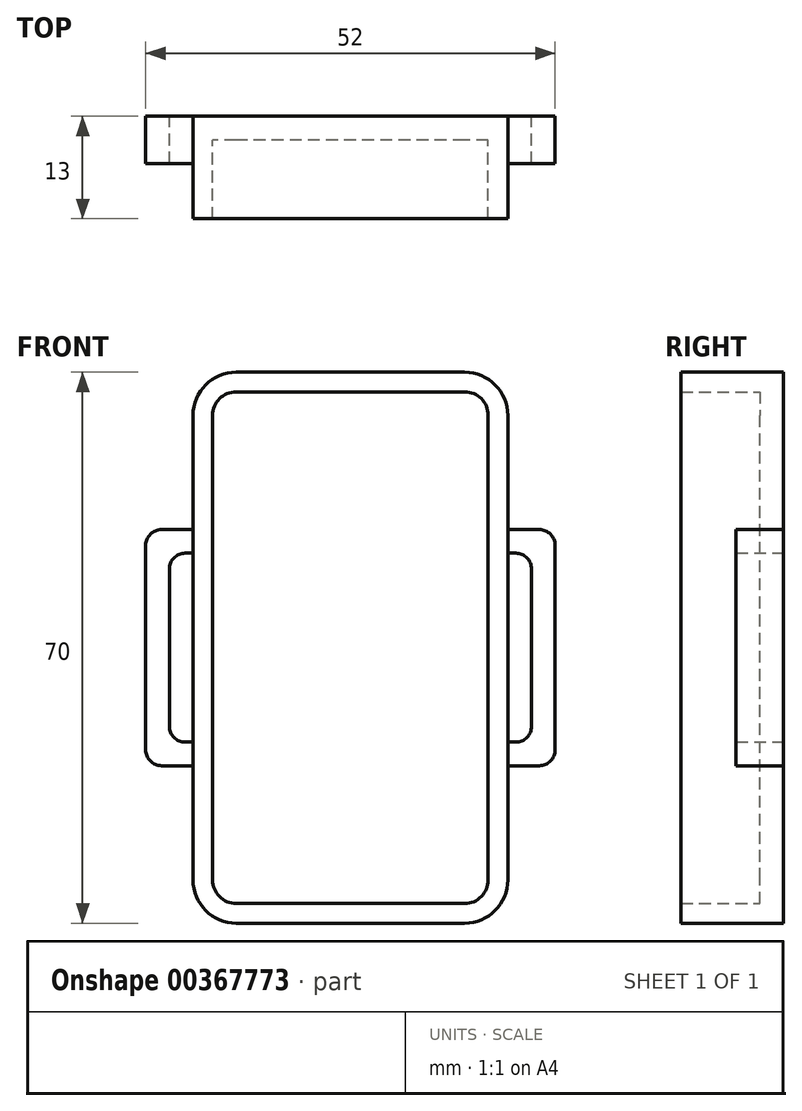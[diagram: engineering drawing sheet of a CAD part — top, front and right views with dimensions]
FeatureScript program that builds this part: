
annotation { "Feature Type Name" : "Feature", "Feature Type Description" : "" }
export const myFeature = defineFeature(function(context is Context, id is Id, definition is map)
    precondition{}
    {
        {
            var Q0;
            Q0=qCreatedBy(makeId("Front.planeOp"),FACE);
            var sketch = newSketch(context, id + "F0", { "sketchPlane" : qUnion([Q0])});
            skLineSegment(sketch, "E0.bottom", {"start": v(14.5, -32.5) * mm, "end": v(-14.5, -32.5) * mm});
            skLineSegment(sketch, "E0.top", {"start": v(14.5, 32.5) * mm, "end": v(-14.5, 32.5) * mm});
            skLineSegment(sketch, "E0.left", {"start": v(17.5, -29.5) * mm, "end": v(17.5, 29.5) * mm});
            skLineSegment(sketch, "E0.right", {"start": v(-17.5, -29.5) * mm, "end": v(-17.5, 29.5) * mm});
            skPoint(sketch, "E0.middle", {"position": v(0, 0) * mm});
            skPoint(sketch, "E1.visualSharp", {"position": v(-17.5, 32.5) * mm});
            skArc(sketch, "E1.filletArc", {"start": v(-14.5, 32.5) * mm, "mid": v(-16.62, 31.62) * mm, "end": v(-17.5, 29.5) * mm});
            skPoint(sketch, "E2.visualSharp", {"position": v(17.5, 32.5) * mm});
            skArc(sketch, "E2.filletArc", {"start": v(17.5, 29.5) * mm, "mid": v(16.62, 31.62) * mm, "end": v(14.5, 32.5) * mm});
            skPoint(sketch, "E3.visualSharp", {"position": v(-17.5, -32.5) * mm});
            skArc(sketch, "E3.filletArc", {"start": v(-17.5, -29.5) * mm, "mid": v(-16.62, -31.62) * mm, "end": v(-14.5, -32.5) * mm});
            skPoint(sketch, "E4.visualSharp", {"position": v(17.5, -32.5) * mm});
            skArc(sketch, "E4.filletArc", {"start": v(14.5, -32.5) * mm, "mid": v(16.62, -31.62) * mm, "end": v(17.5, -29.5) * mm});
            skArc(sketch, "E5.0", {"start": v(-14.5, 35) * mm, "mid": v(-18.39, 33.39) * mm, "end": v(-20, 29.5) * mm});
            skLineSegment(sketch, "E6.0", {"start": v(14.5, 35) * mm, "end": v(-14.5, 35) * mm});
            skArc(sketch, "E7.0", {"start": v(20, 29.5) * mm, "mid": v(18.39, 33.39) * mm, "end": v(14.5, 35) * mm});
            skLineSegment(sketch, "E8.0", {"start": v(-20, -29.5) * mm, "end": v(-20, 29.5) * mm});
            skLineSegment(sketch, "E9.0", {"start": v(20, -29.5) * mm, "end": v(20, 29.5) * mm});
            skArc(sketch, "E10.0", {"start": v(-20, -29.5) * mm, "mid": v(-18.39, -33.39) * mm, "end": v(-14.5, -35) * mm});
            skLineSegment(sketch, "E11.0", {"start": v(14.5, -35) * mm, "end": v(-14.5, -35) * mm});
            skArc(sketch, "E12.0", {"start": v(14.5, -35) * mm, "mid": v(18.39, -33.39) * mm, "end": v(20, -29.5) * mm});
            skLineSegment(sketch, "E13.bottom", {"start": v(-20, -15) * mm, "end": v(-24, -15) * mm});
            skLineSegment(sketch, "E13.top", {"start": v(-20, 15) * mm, "end": v(-24, 15) * mm});
            skLineSegment(sketch, "E13.left", {"start": v(-20, -15) * mm, "end": v(-20, -12) * mm});
            skLineSegment(sketch, "E13.right", {"start": v(-26, -13) * mm, "end": v(-26, 13) * mm});
            skPoint(sketch, "E13.middle", {"position": v(-23, 0) * mm});
            skLineSegment(sketch, "E14.0", {"start": v(-20, 12) * mm, "end": v(-21, 12) * mm});
            skLineSegment(sketch, "E15.0", {"start": v(-23, -10) * mm, "end": v(-23, 10) * mm});
            skLineSegment(sketch, "E16.trimOffspring", {"start": v(-20, 12) * mm, "end": v(-20, 15) * mm});
            skLineSegment(sketch, "E17", {"start": v(-21, -12) * mm, "end": v(-20, -12) * mm});
            skPoint(sketch, "E18.MirrorP", {"position": v(23, 0) * mm});
            skLineSegment(sketch, "E19.MirrorCS", {"start": v(20, 12) * mm, "end": v(21, 12) * mm});
            skLineSegment(sketch, "E20.MirrorCS", {"start": v(20, -15) * mm, "end": v(24, -15) * mm});
            skLineSegment(sketch, "E21.MirrorCS", {"start": v(23, -10) * mm, "end": v(23, 10) * mm});
            skLineSegment(sketch, "E22.MirrorCS", {"start": v(21, -12) * mm, "end": v(20, -12) * mm});
            skLineSegment(sketch, "E23.MirrorCS", {"start": v(20, 15) * mm, "end": v(24, 15) * mm});
            skLineSegment(sketch, "E24.MirrorCS", {"start": v(26, -13) * mm, "end": v(26, 13) * mm});
            skPoint(sketch, "E25.visualSharp", {"position": v(-26, 15) * mm});
            skArc(sketch, "E25.filletArc", {"start": v(-24, 15) * mm, "mid": v(-25.41, 14.41) * mm, "end": v(-26, 13) * mm});
            skPoint(sketch, "E26.visualSharp", {"position": v(-26, -15) * mm});
            skArc(sketch, "E26.filletArc", {"start": v(-26, -13) * mm, "mid": v(-25.41, -14.41) * mm, "end": v(-24, -15) * mm});
            skPoint(sketch, "E27.visualSharp", {"position": v(26, 15) * mm});
            skArc(sketch, "E27.filletArc", {"start": v(26, 13) * mm, "mid": v(25.41, 14.41) * mm, "end": v(24, 15) * mm});
            skPoint(sketch, "E28.visualSharp", {"position": v(26, -15) * mm});
            skArc(sketch, "E28.filletArc", {"start": v(24, -15) * mm, "mid": v(25.41, -14.41) * mm, "end": v(26, -13) * mm});
            skPoint(sketch, "E29.visualSharp", {"position": v(-23, 12) * mm});
            skArc(sketch, "E29.filletArc", {"start": v(-21, 12) * mm, "mid": v(-22.41, 11.41) * mm, "end": v(-23, 10) * mm});
            skPoint(sketch, "E30.visualSharp", {"position": v(-23, -12) * mm});
            skArc(sketch, "E30.filletArc", {"start": v(-23, -10) * mm, "mid": v(-22.41, -11.41) * mm, "end": v(-21, -12) * mm});
            skPoint(sketch, "E31.visualSharp", {"position": v(23, 12) * mm});
            skArc(sketch, "E31.filletArc", {"start": v(23, 10) * mm, "mid": v(22.41, 11.41) * mm, "end": v(21, 12) * mm});
            skPoint(sketch, "E32.visualSharp", {"position": v(23, -12) * mm});
            skArc(sketch, "E32.filletArc", {"start": v(21, -12) * mm, "mid": v(22.41, -11.41) * mm, "end": v(23, -10) * mm});
            skSolve(sketch);
        }
        {
            var Q0;
            Q0=makeQuery(id+"F0.imprint","IMPRINT",FACE,{"disambiguationData":[TD([[makeQuery(id+"F0.imprint","IMPRINT",EDGE,{"derivedFrom":sQuery(id+"F0.wireOp",EDGE,"E0.bottom")}),-1.0]])]});
            extrude(context, id + "F1", {"entities" : qUnion([Q0]), "depth" : 3 * mm});
        }
        {
            var Q0;
            Q0=makeQuery(id+"F0.imprint","IMPRINT",FACE,{"disambiguationData":[TD([[makeQuery(id+"F0.imprint","IMPRINT",EDGE,{"derivedFrom":sQuery(id+"F0.wireOp",EDGE,"E0.bottom")}),1.0]])]});
            extrude(context, id + "F2", {"entities" : qUnion([Q0]), "operationType" : NewBodyOperationType.ADD, "depth" : 13 * mm});
        }
        {
            var Q0;
            Q0=makeQuery(id+"F0.imprint","IMPRINT",FACE,{"disambiguationData":[TD([[makeQuery(id+"F0.imprint","IMPRINT",EDGE,{"derivedFrom":sQuery(id+"F0.wireOp",EDGE,"E13.bottom")}),-1.0]])]});
            var Q1;
            {var subQ1=sQuery(id+"F0.wireOp",EDGE,"E19.MirrorCS");Q1=makeQuery(id+"F0.imprint","IMPRINT",FACE,{"disambiguationData":[TD([[makeQuery(id+"F0.imprint","IMPRINT",EDGE,{"derivedFrom":subQ1}),1.0]])]});}
            extrude(context, id + "F3", {"entities" : qUnion([Q0, Q1]), "operationType" : NewBodyOperationType.ADD, "depth" : 6 * mm});
        }
    });
